# Revit family: Lobby Door 1150x750
name_source: partatom
category: Generic Models
revit_build: Autodesk Revit 2018 (Build: 20190510_1515(x64)
units: mm (PartAtom-declared; Revit-internal decimal feet)

## family parameters
Always vertical = No
Can host rebar = No
Cut with Voids When Loaded = No
OmniClass Number = 23.30.40.11
OmniClass Title = Hardware for Doors
Part Type = Normal
Room Calculation Point = No
Round Connector Dimension = Use Diameter
Shared = No
Work Plane-Based = Yes

## types (1)
- Controls
    BIMObject Category_2 = Fire Doors
    BIMobject category = Damper
    Colour = Powder Coated to RAL 9010 - White
    Cost = 0 $
    Default Elevation = 1219 mm
    Depth = 100 mm  [stored 0.328084 ft]
    Description = The unit is dual purpose, providing fire rating (tested to FD30s/E30s) while closed, and smoke ventilation when in the open position. - See more at: http://easivent.co.uk
    Design country = UK
    Edition number = 1
    Height = 750 mm  [stored 2.46063 ft]
    IFC Classification = Damper
    IP rating = FD30S
    Keynote = This lobby vent has been designed to meet the requirements of both UL555 (fire) and UL55S (high temperature smoke). - See more at: http://easivent.co.uk
    Manufacturer = Easivent
    Manufacturer URL = http://easivent.co.uk
    Manufacturer country = UK
    Manufacturer name = Easivent
    Material Main = Powder Coated Zintec Steel
    Model = E-Vent Smoke Shaft Vent
    Nominal height = 750
    Nominal width = 1150
    Notes = Please note this product may be amended without prior notification
    Product SKU = Smoke Shaft AOV to E30s
    Product data URL = http://easivent.co.uk
    Product family = Fire Door
    Product group = Lobby Ventilator
    SerialNumber = 0
    Size = 1150x750x100mm (W x D x H)
    TagNumber = 0
    Technical description = Free area 0.6m2
    Type Comments = (high temperature smoke).
The unit is dual purpose, providing fire rating
(tested to FD30s/E30s) while closed, and
smoke ventilation when in the open position.
    UNSPSC Code = 40101504
    UNSPSC name = Ventilation dampers
    Uniclass 2.0 Code = Pr_70_65_82_64
    Uniclass 2.0 Description = Shut Off Damper
    WarrantyDuration = 12
    WarrantyStartDate = From items dispatch
    Weight Net (Kg) = 0
    Width = 1150
    switch-on-duration = To be controlled via chain drive acutator

note: [stored X ft] marks values corroborated as IEEE doubles in the binary element streams (Revit-internal decimal feet)

## geometry (parser evidence)
native form markers: Sweep x7
no freeform markers — native parametric forms only
